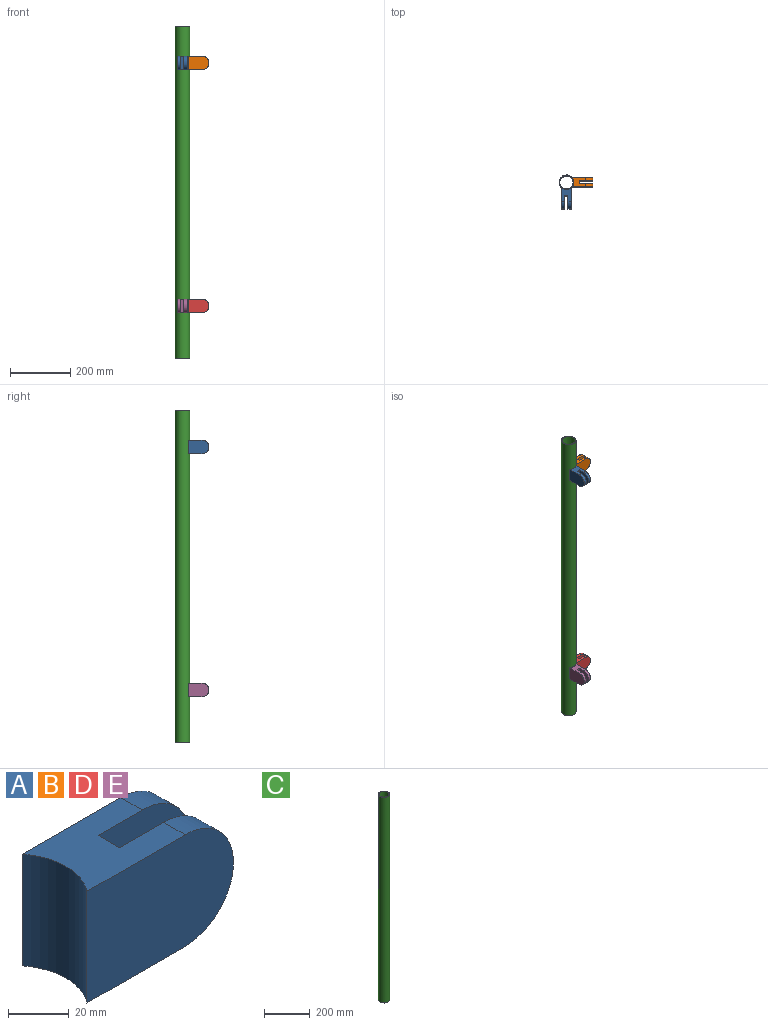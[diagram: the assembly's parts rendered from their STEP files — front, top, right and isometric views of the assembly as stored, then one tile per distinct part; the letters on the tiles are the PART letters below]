
ASSEMBLY  parts=5 mates=4
PART A: 10 faces, bbox 68.2x30x45 mm
  f0: plane 45x43mm, normal (0,-1,0), area 1717.7mm2, adj f5,f6,f7,f9
  f1: plane 68.22x45mm, normal (0,1,0), area 2852.8mm2, adj f4,f6,f7,f9
  f2: plane 68.22x45mm, normal (0,-1,0), area 2852.8mm2, adj f4,f6,f7,f8
  f3: plane 45x43mm, normal (0,1,0), area 1717.7mm2, adj f5,f6,f7,f8
  f4: cylinder r=24.15mm len=45mm, axis (0,0,-1), area 1456.6mm2, adj f1,f2,f6,f7
  f5: plane 45x10mm, normal (1,0,0), area 450mm2, adj f0,f3,f6,f7
  f6: plane 45.72x30mm, normal (0,0,1), area 1059.7mm2, adj f0,f1,f2,f3,f4,f5,f8,f9
  f7: plane 45.72x30mm, normal (0,0,-1), area 1059.7mm2, adj f0,f1,f2,f3,f4,f5,f8,f9
  f8: cylinder r=22.5mm len=45mm, axis (0,-1,0), area 706.9mm2, adj f2,f3,f6,f7
  f9: cylinder r=22.5mm len=45mm, axis (0,-1,0), area 706.9mm2, adj f0,f1,f6,f7
PART B: same geometry as A
PART C: 4 faces, bbox 48.3x48.3x1100 mm
  f0: cylinder r=22.15mm len=1100mm, axis (0,0,-1), area 153089.8mm2, adj f2,f3
  f1: cylinder r=24.15mm len=1100mm, axis (0,0,-1), area 166912.8mm2, adj f2,f3
  f2: plane 48.3x48.3mm, normal (0,0,1), area 290.9mm2, adj f0,f1
  f3: plane 48.3x48.3mm, normal (0,0,-1), area 290.9mm2, adj f0,f1
PART D: same geometry as A
PART E: same geometry as A
PLACE A rot(axis=(0,0,-1),90deg) t=(0,0,955)mm
PLACE B rot(axis=(1,0,0),180deg) t=(0,0,1000)mm
PLACE C at identity fixed
PLACE D t=(0,0,150)mm
PLACE E rot(axis=(0,0,-1),90deg) t=(0,0,150)mm
MATE fastened A.f4 <-> C.f1  axis (0,0,-1) through (0,0,977.5)mm
MATE fastened C.f1 <-> D.f4  axis (0,0,-1) through (0,0,550)mm
MATE fastened B.f4 <-> C.f1  axis (0,0,1) through (0,0,977.5)mm
MATE fastened E.f4 <-> C.f1  axis (0,0,-1) through (0,0,172.5)mm
